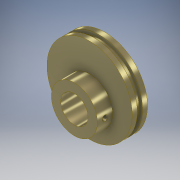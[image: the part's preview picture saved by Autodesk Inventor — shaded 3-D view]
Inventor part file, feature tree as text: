
AUTODESK INVENTOR PART (.ipt)
format: ipt  version: 2017 (Build 210142000, 142)  size: 174,592 bytes
history: native  units: mm
features: extrude x7, sketch x6, projected_geometry x2, plane x1
ambient origin geometry x8: Origin, YZ Plane, XZ Plane, XY Plane, X Axis, Y Axis, Z Axis, Center Point
bodies: Solid1 (feature_tree)
feature tree (16):
  extrude  "Extrusion1"  Depth=1.5mm TaperAngle=0.0deg
  extrude  "Extrusion2"  Depth=1.5mm TaperAngle=0.0deg
  extrude  "Extrusion3"  Depth=1.5mm TaperAngle=0.0deg
  sketch  "Sketch4"  dims[d9=3.0mm d17=13.5mm]
  extrude  "Extrusion6"  Depth=3.0mm
  extrude  "Extrusion7"  Depth=4.45mm TaperAngle=0.0deg
  plane  "Work Plane1"
  extrude  "Extrusion8"  Depth=10.0mm
  extrude  "Extrusion10"  Depth=10.0mm
  sketch  "Sketch1"  dims[d0=23.0mm d1=1.5mm d2=0.0mm]
  sketch  "Sketch2"  dims[d3=25.0mm d4=1.5mm d5=0.0mm]
  sketch  "Sketch3"  dims[d6=25.0mm d7=1.5mm d8=0.0mm]
  projected_geometry  "Projected Loop1"
  sketch  "Sketch6"  dims[d18=8.0mm d19=4.45mm d20=0.0mm]
  projected_geometry  "Projected Loop2"
  sketch  "Sketch7"  dims[d21=10.0mm d22=0.0mm d23=6.76mm d24=4.45mm d25=13.5mm d26=6.75mm d27=2.225mm d28=10.0mm d29=1.6mm d30=4.45mm d31=0.0mm d32=22.0mm d35=0.2mm d36=0.0mm]
